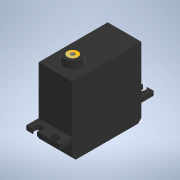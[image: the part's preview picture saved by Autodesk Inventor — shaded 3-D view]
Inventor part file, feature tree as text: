
AUTODESK INVENTOR PART (.ipt)
format: ipt  version: 2020 (Build 240168000, 168)  size: 210,432 bytes
history: native  units: mm
features: sketch x9, extrude x7, projected_geometry x6, other x2, hole x2, chamfer x2
ambient origin geometry x8: Origin, YZ Plane, XZ Plane, XY Plane, X Axis, Y Axis, Z Axis, Center Point
bodies: Body1 (feature_tree), Body2 (feature_tree)
feature tree (28):
  other  "솔리드1"
  extrude  "돌출1"  Depth=19.5mm
  extrude  "돌출2"  Depth=40.0mm
  extrude  "돌출3"  Depth=40.0mm TaperAngle=0.0deg
  extrude  "돌출4"  Depth=10.0mm
  hole  "구멍1"  [1 undecoded]
  extrude  "돌출5"  Depth=4.0mm TaperAngle=0.0deg
  chamfer  "모따기1"  Distance=6.0mm
  chamfer  "모따기2"  Distance=4.0mm
  extrude  "돌출8"  Depth=4.0mm TaperAngle=0.0deg
  extrude  "돌출9"  Depth=14.0mm
  hole  "구멍2"  [1 undecoded]
  sketch  "스케치1"
  sketch  "스케치2"
  projected_geometry  "투영된 루프1"
  sketch  "스케치3"
  sketch  "스케치4"
  projected_geometry  "투영된 루프2"
  other  "솔리드2"
  sketch  "스케치5"
  projected_geometry  "투영된 루프3"
  sketch  "스케치6"
  sketch  "스케치9"
  sketch  "스케치10"
  projected_geometry  "투영된 루프4"
  sketch  "스케치12"
  projected_geometry  "투영된 루프5"
  projected_geometry  "투영된 루프6"
note: 2 required parameter values undecoded (feature->parameter linkage not recoverable at this tier; creation-order binding heuristic only, values carry confidence <= 0.55)
